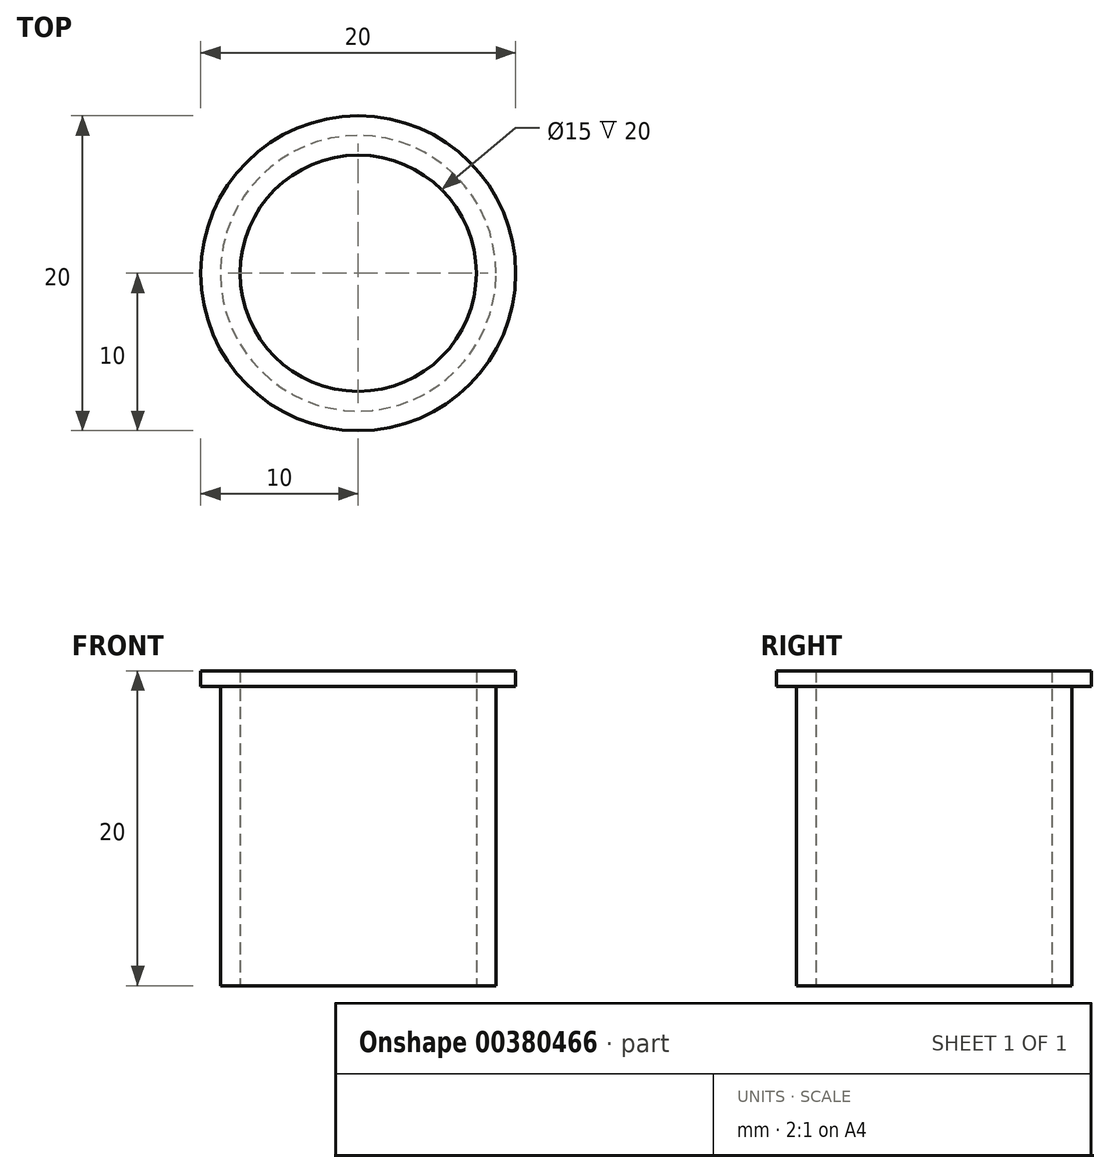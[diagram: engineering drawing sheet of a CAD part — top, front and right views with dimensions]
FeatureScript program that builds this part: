
annotation { "Feature Type Name" : "Feature", "Feature Type Description" : "" }
export const myFeature = defineFeature(function(context is Context, id is Id, definition is map)
    precondition{}
    {
        {
            var Q0;
            Q0=qCreatedBy(makeId("Top.planeOp"),FACE);
            var sketch = newSketch(context, id + "F0", { "sketchPlane" : qUnion([Q0])});
            skCircle(sketch, "E0", {"center": v(0, 0) * mm, "radius": 8.75 * mm});
            skSolve(sketch);
        }
        {
            var Q0;
            Q0 = qSketchRegion(id + "F0", true);
            extrude(context, id + "F1", {"entities" : qUnion([Q0]), "depth" : 19 * mm});
        }
        {
            var Q0;
            Q0=makeQuery(id+"F1.opExtrude","CAP_FACE",FACE,{"disambiguationData":[OSD([sQuery(id+"F0.wireOp",EDGE,"E0")])],"isStart":false});
            var Q1;
            Q1=makeQuery(id+"F1.opExtrude","CAP_FACE",FACE,{"disambiguationData":[OSD([sQuery(id+"F0.wireOp",EDGE,"E0")])],"isStart":true});
            shell(context, id + "F2", {"entities" : qUnion([Q0, Q1]), "thickness" : 1.25 * mm});
        }
        {
            var Q0;
            Q0=makeQuery(id+"F1.opExtrude","CAP_FACE",FACE,{"disambiguationData":[OSD([sQuery(id+"F0.wireOp",EDGE,"E0")])],"isStart":false});
            var sketch = newSketch(context, id + "F3", { "sketchPlane" : qUnion([Q0])});
            skCircle(sketch, "E1", {"center": v(0, 0) * mm, "radius": 10 * mm});
            skSolve(sketch);
        }
        {
            var Q0;
            Q0 = qSketchRegion(id + "F3", true);
            extrude(context, id + "F4", {"entities" : qUnion([Q0]), "operationType" : NewBodyOperationType.ADD, "depth" : 1 * mm});
        }
        {
            var Q0;
            Q0=makeQuery(id+"F4.boolean.opBoolean","SPLIT",FACE,{"disambiguationData":[TD([makeQuery(id+"F2.opShell","OFFSET_FACE",FACE,{"disambiguationData":[OSD([sQuery(id+"F0.wireOp",EDGE,"E0")])]})])],"derivedFrom":makeQuery(id+"F4.opExtrude","CAP_FACE",FACE,{"disambiguationData":[OSD([sQuery(id+"F3.wireOp",EDGE,"E1")])],"isStart":true})});
            var sketch = newSketch(context, id + "F5", { "sketchPlane" : qUnion([Q0])});
            skCircle(sketch, "E2", {"center": v(0, 0) * mm, "radius": 7.5 * mm});
            skSolve(sketch);
        }
        {
            var Q0;
            Q0 = qSketchRegion(id + "F5", true);
            extrude(context, id + "F6", {"entities" : qUnion([Q0]), "operationType" : NewBodyOperationType.REMOVE, "endBound" : BoundingType.THROUGH_ALL, "oppositeDirection" : true, "depth" : 25 * mm});
        }
    });
